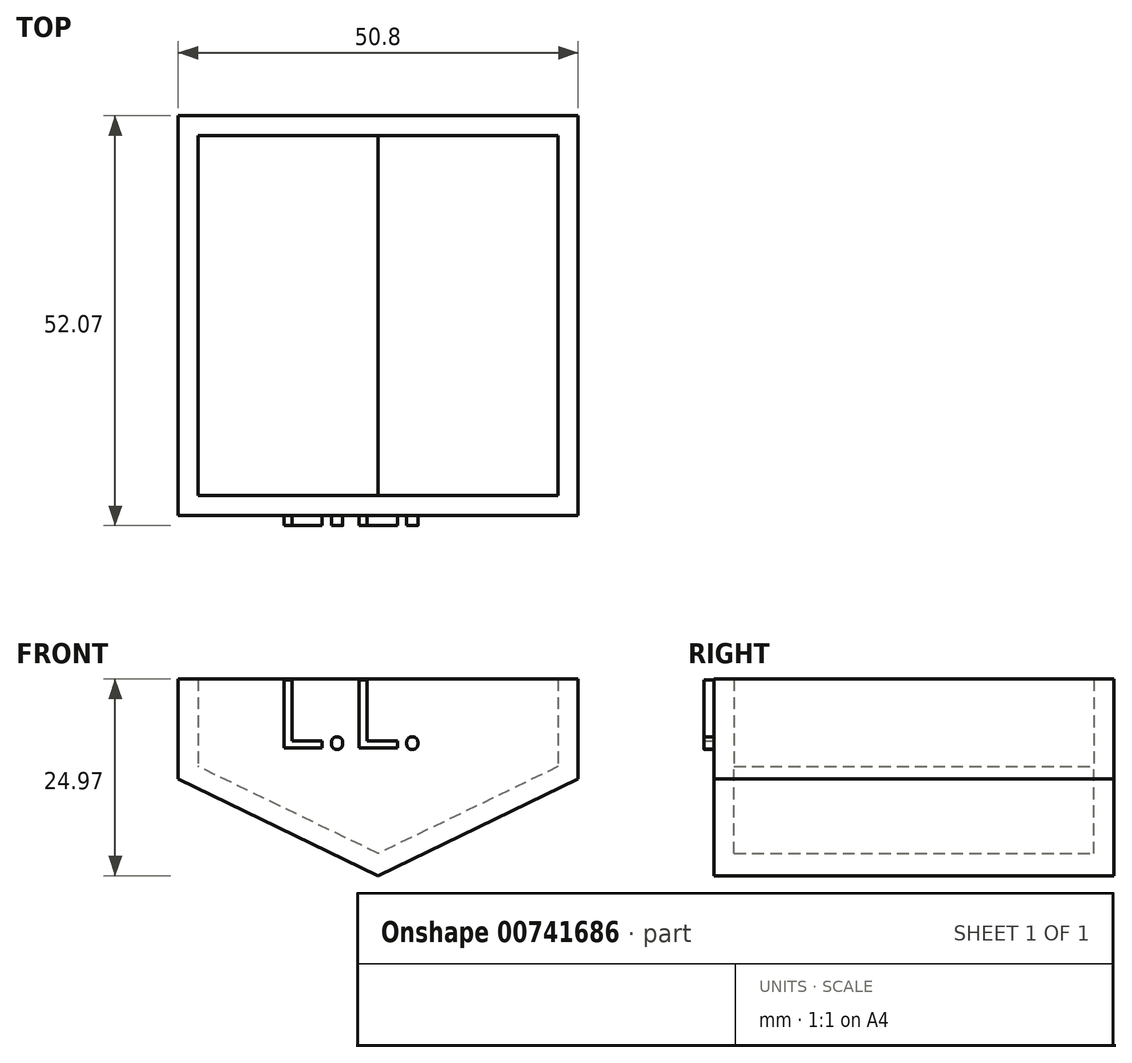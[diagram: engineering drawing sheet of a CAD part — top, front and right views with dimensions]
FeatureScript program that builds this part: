
annotation { "Feature Type Name" : "Feature", "Feature Type Description" : "" }
export const myFeature = defineFeature(function(context is Context, id is Id, definition is map)
    precondition{}
    {
        {
            var Q0;
            Q0=qCreatedBy(makeId("Front.planeOp"),FACE);
            var sketch = newSketch(context, id + "F0", { "sketchPlane" : qUnion([Q0])});
            skLineSegment(sketch, "E0", {"start": v(-64.1, 8.76) * mm, "end": v(-64.1, -3.94) * mm});
            skLineSegment(sketch, "E1", {"start": v(-64.1, 8.76) * mm, "end": v(-13.3, 8.76) * mm});
            skLineSegment(sketch, "E2", {"start": v(-13.3, 8.76) * mm, "end": v(-13.3, -3.94) * mm});
            skLineSegment(sketch, "E3", {"start": v(-13.3, -3.94) * mm, "end": v(-38.7, -16.2) * mm});
            skPoint(sketch, "E3.endSnap0", {"position": v(-38.7, 8.76) * mm});
            skLineSegment(sketch, "E4", {"start": v(-38.7, -16.2) * mm, "end": v(-64.1, -3.94) * mm});
            skSolve(sketch);
        }
        {
            var Q0;
            Q0=makeQuery(id+"F0.imprint","IMPRINT",FACE,{"disambiguationData":[TD([[makeQuery(id+"F0.imprint","IMPRINT",EDGE,{"derivedFrom":sQuery(id+"F0.wireOp",EDGE,"E0")}),1.0]])]});
            extrude(context, id + "F1", {"entities" : qUnion([Q0]), "depth" : 50.8 * mm, "offsetDistance" : 25.4 * mm});
        }
        {
            var Q0;
            Q0=makeQuery(id+"F1.opExtrude","SWEPT_FACE",FACE,{"disambiguationData":[OSD([sQuery(id+"F0.wireOp",EDGE,"E1")])]});
            shell(context, id + "F2", {"entities" : qUnion([Q0]), "thickness" : 2.54 * mm});
        }
        {
            var Q0;
            Q0=makeQuery(id+"F1.opExtrude","CAP_FACE",FACE,{"disambiguationData":[OSD([sQuery(id+"F0.wireOp",EDGE,"E0"),sQuery(id+"F0.wireOp",EDGE,"E1"),sQuery(id+"F0.wireOp",EDGE,"E2"),sQuery(id+"F0.wireOp",EDGE,"E3"),sQuery(id+"F0.wireOp",EDGE,"E4")])],"isStart":false});
            var sketch = newSketch(context, id + "F3", { "sketchPlane" : qUnion([Q0])});
            skText(sketch, "E5", { "text": "L.L.", "fontName": "OpenSans-Regular.ttf"});
            const initialGuessF3  = {"E5": [-0.05185, 0, 1, 0, 0.00876]};
            skSetInitialGuess(sketch, initialGuessF3);
            skSolve(sketch);
        }
        {
            var Q0;
            Q0 = qSketchRegion(id + "F3", true);
            extrude(context, id + "F4", {"entities" : qUnion([Q0]), "operationType" : NewBodyOperationType.ADD, "depth" : 1.27 * mm, "offsetDistance" : 25.4 * mm});
        }
    });
